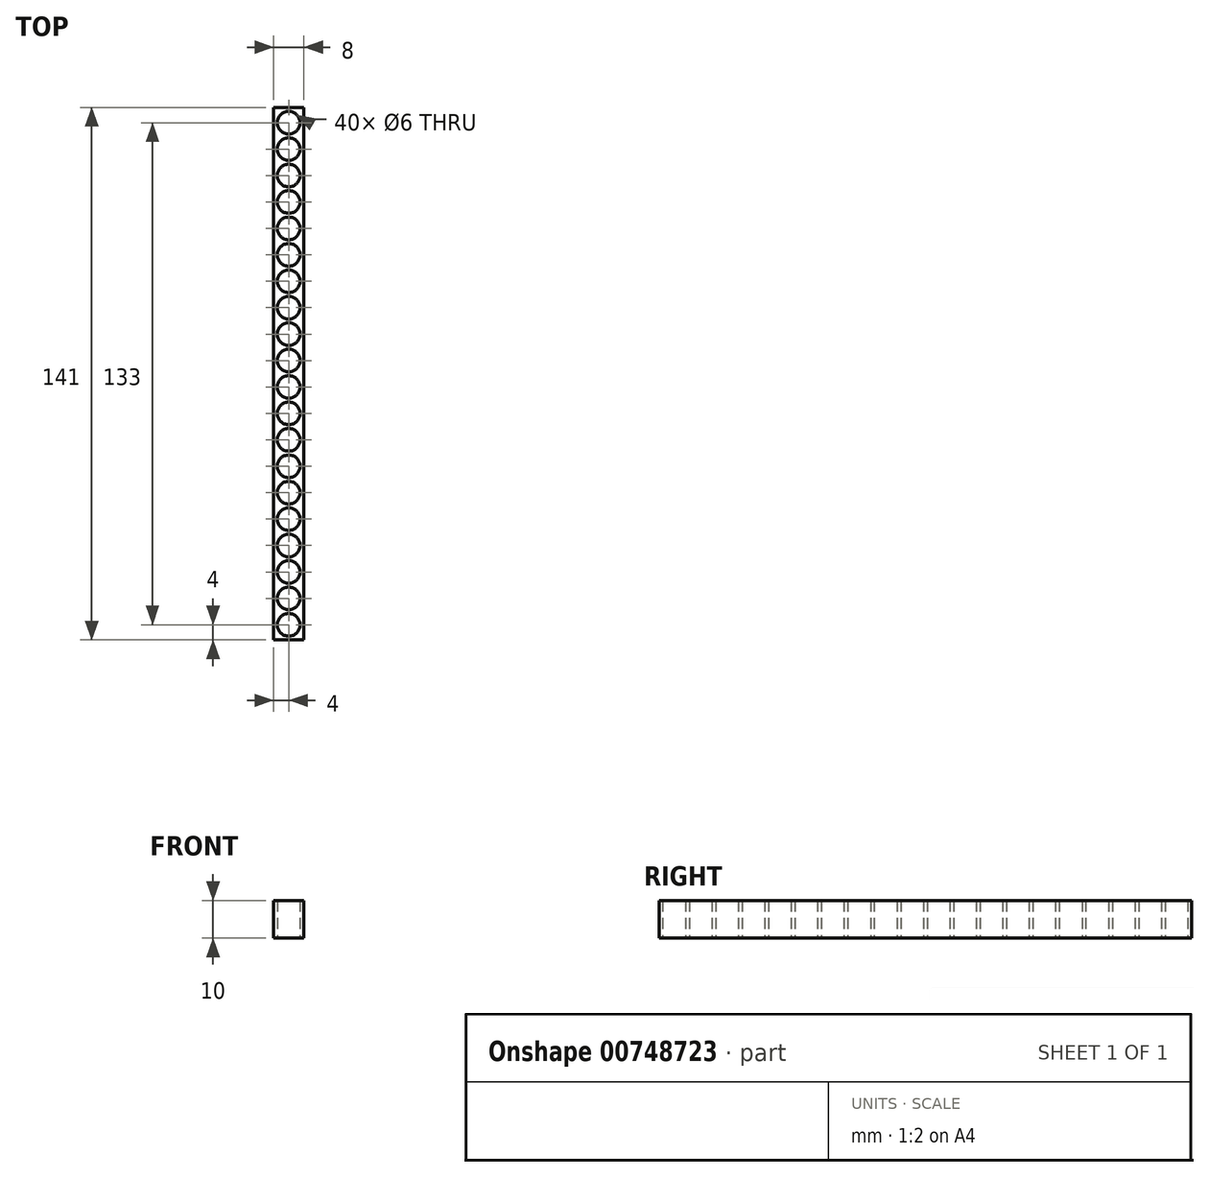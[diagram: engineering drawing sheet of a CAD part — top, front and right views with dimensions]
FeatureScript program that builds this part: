
annotation { "Feature Type Name" : "Feature", "Feature Type Description" : "" }
export const myFeature = defineFeature(function(context is Context, id is Id, definition is map)
    precondition{}
    {
        {
            var Q0;
            Q0=qCreatedBy(makeId("Top.planeOp"),FACE);
            var sketch = newSketch(context, id + "F0", { "sketchPlane" : qUnion([Q0])});
            skLineSegment(sketch, "E0.bottom", {"start": v(4, 70.5) * mm, "end": v(-4, 70.5) * mm});
            skLineSegment(sketch, "E0.top", {"start": v(4, -70.5) * mm, "end": v(-4, -70.5) * mm});
            skLineSegment(sketch, "E0.left", {"start": v(4, 70.5) * mm, "end": v(4, -70.5) * mm});
            skLineSegment(sketch, "E0.right", {"start": v(-4, 70.5) * mm, "end": v(-4, -70.5) * mm});
            skPoint(sketch, "E0.middle", {"position": v(0, 0) * mm});
            skCircle(sketch, "E1", {"center": v(0, 66.5) * mm, "radius": 3 * mm});
            skCircle(sketch, "E2.0.1.0", {"center": v(0, 59.5) * mm, "radius": 3 * mm});
            skCircle(sketch, "E2.0.2.0", {"center": v(0, 52.5) * mm, "radius": 3 * mm});
            skCircle(sketch, "E2.0.3.0", {"center": v(0, 45.5) * mm, "radius": 3 * mm});
            skCircle(sketch, "E2.0.4.0", {"center": v(0, 38.5) * mm, "radius": 3 * mm});
            skCircle(sketch, "E2.0.5.0", {"center": v(0, 31.5) * mm, "radius": 3 * mm});
            skCircle(sketch, "E2.0.6.0", {"center": v(0, 24.5) * mm, "radius": 3 * mm});
            skCircle(sketch, "E2.0.7.0", {"center": v(0, 17.5) * mm, "radius": 3 * mm});
            skCircle(sketch, "E2.0.8.0", {"center": v(0, 10.5) * mm, "radius": 3 * mm});
            skCircle(sketch, "E2.0.9.0", {"center": v(0, 3.5) * mm, "radius": 3 * mm});
            skCircle(sketch, "E2.0.10.0", {"center": v(0, -3.5) * mm, "radius": 3 * mm});
            skCircle(sketch, "E2.0.11.0", {"center": v(0, -10.5) * mm, "radius": 3 * mm});
            skCircle(sketch, "E2.0.12.0", {"center": v(0, -17.5) * mm, "radius": 3 * mm});
            skCircle(sketch, "E2.0.13.0", {"center": v(0, -24.5) * mm, "radius": 3 * mm});
            skCircle(sketch, "E2.0.14.0", {"center": v(0, -31.5) * mm, "radius": 3 * mm});
            skCircle(sketch, "E2.0.15.0", {"center": v(0, -38.5) * mm, "radius": 3 * mm});
            skCircle(sketch, "E2.0.16.0", {"center": v(0, -45.5) * mm, "radius": 3 * mm});
            skCircle(sketch, "E2.0.17.0", {"center": v(0, -52.5) * mm, "radius": 3 * mm});
            skCircle(sketch, "E2.0.18.0", {"center": v(0, -59.5) * mm, "radius": 3 * mm});
            skCircle(sketch, "E2.0.19.0", {"center": v(0, -66.5) * mm, "radius": 3 * mm});
            skLineSegment(sketch, "E2.direction1", {"start": v(0, 66.5) * mm, "end": v(48.75, 66.5) * mm, "construction": true});
            skLineSegment(sketch, "E2.direction2", {"start": v(0, 66.5) * mm, "end": v(0, 59.5) * mm, "construction": true});
            skSolve(sketch);
        }
        {
            var Q0;
            Q0 = qSketchRegion(id + "F0", true);
            extrude(context, id + "F1", {"entities" : qUnion([Q0]), "depth" : 10 * mm, "offsetDistance" : 25 * mm});
        }
    });
